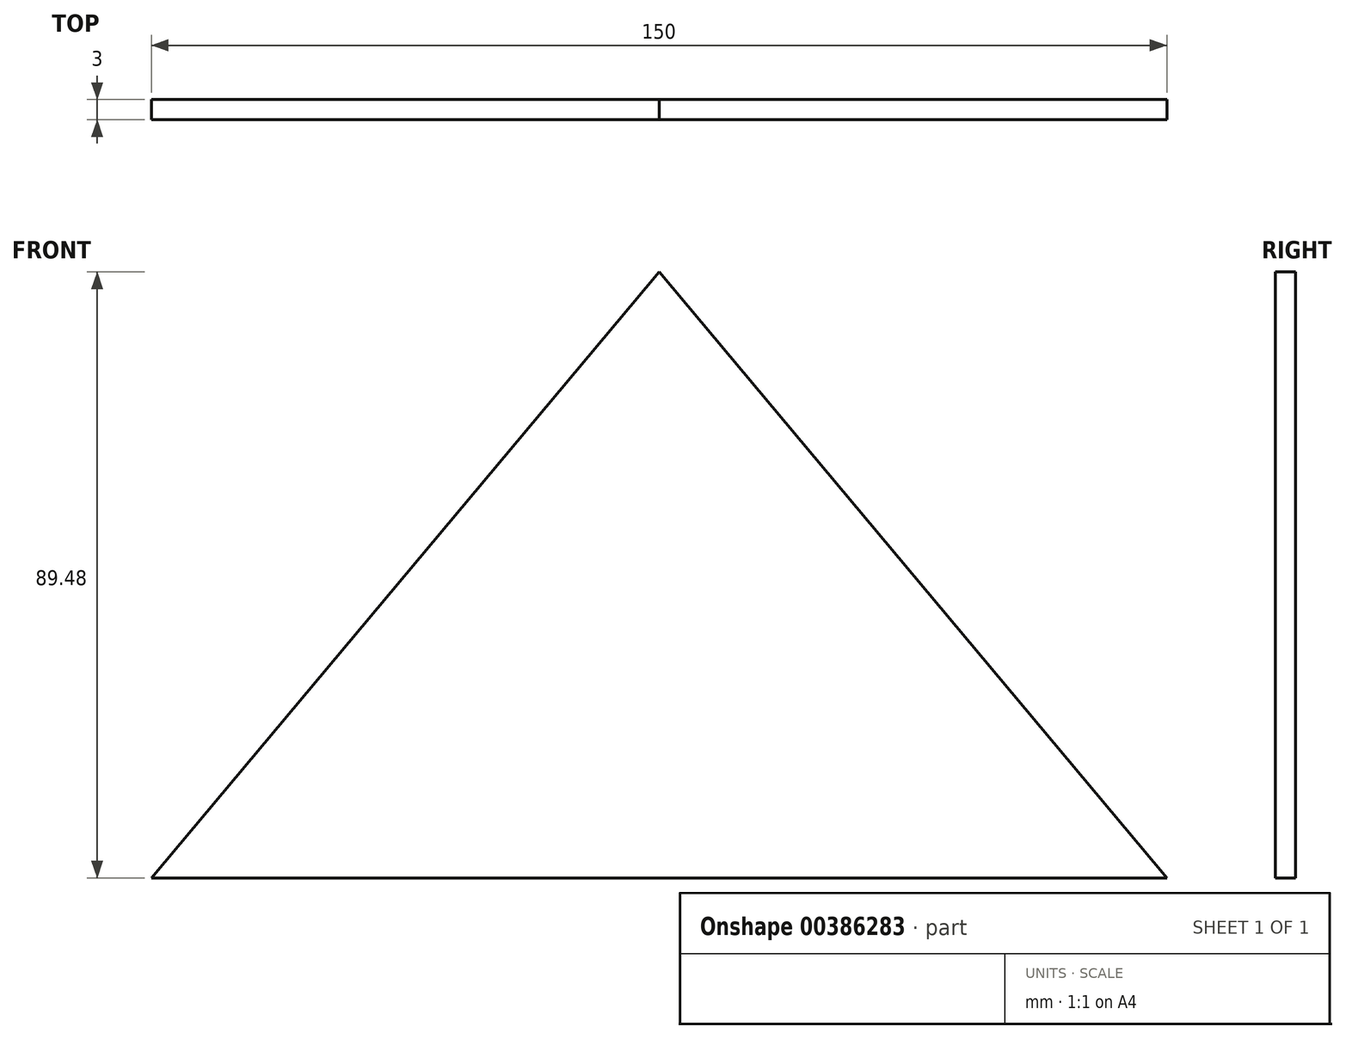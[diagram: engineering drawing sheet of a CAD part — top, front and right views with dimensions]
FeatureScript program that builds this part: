
annotation { "Feature Type Name" : "Feature", "Feature Type Description" : "" }
export const myFeature = defineFeature(function(context is Context, id is Id, definition is map)
    precondition{}
    {
        {
            var Q0;
            Q0=qCreatedBy(makeId("Front.planeOp"),FACE);
            var sketch = newSketch(context, id + "F0", { "sketchPlane" : qUnion([Q0])});
            skCircle(sketch, "E0.cCircle", {"center": v(0, 78.7) * mm, "radius": 35 * mm, "construction": true});
            skLineSegment(sketch, "E0.0", {"start": v(75, 43.7) * mm, "end": v(-75, 43.7) * mm});
            skLineSegment(sketch, "E0.1", {"start": v(-75, 43.7) * mm, "end": v(0, 133.2) * mm});
            skLineSegment(sketch, "E0.2", {"start": v(0, 133.2) * mm, "end": v(75, 43.7) * mm});
            skPoint(sketch, "E0.0.midPoint", {"position": v(0, 43.7) * mm});
            skLineSegment(sketch, "E1.bottom", {"start": v(-75, 43.7) * mm, "end": v(75, 43.7) * mm});
            skLineSegment(sketch, "E1.top", {"start": v(-75, -56.3) * mm, "end": v(75, -56.3) * mm});
            skLineSegment(sketch, "E1.left", {"start": v(-75, 43.7) * mm, "end": v(-75, -56.3) * mm});
            skLineSegment(sketch, "E1.right", {"start": v(75, 43.7) * mm, "end": v(75, -56.3) * mm});
            skSolve(sketch);
        }
        {
            var Q0;
            Q0=makeQuery(id+"F0.imprint","IMPRINT",FACE,{"disambiguationData":[TD([[makeQuery(id+"F0.imprint","IMPRINT",EDGE,{"derivedFrom":sQuery(id+"F0.wireOp",EDGE,"E1.bottom")}),-1.0]])]});
            var Q1;
            Q1=makeQuery(id+"F0.imprint","IMPRINT",FACE,{"disambiguationData":[TD([[makeQuery(id+"F0.imprint","IMPRINT",EDGE,{"derivedFrom":sQuery(id+"F0.wireOp",EDGE,"E0.1")}),-1.0]])]});
            extrude(context, id + "F1", {"entities" : qUnion([Q0, Q1]), "depth" : 3 * mm});
        }
    });
